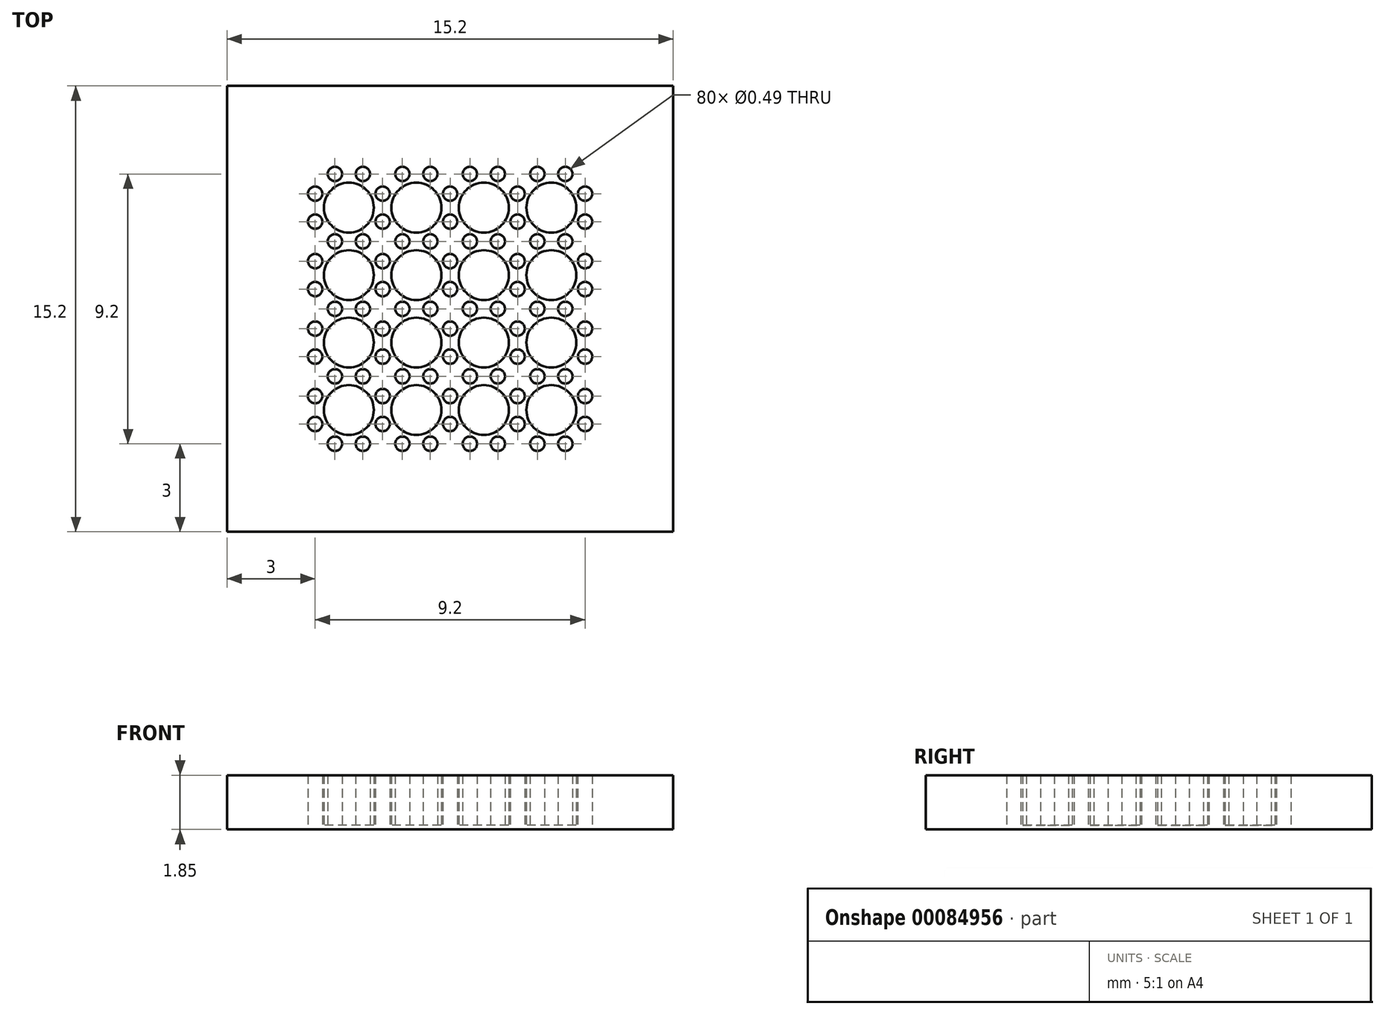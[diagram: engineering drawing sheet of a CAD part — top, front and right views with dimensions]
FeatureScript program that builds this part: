
annotation { "Feature Type Name" : "Feature", "Feature Type Description" : "" }
export const myFeature = defineFeature(function(context is Context, id is Id, definition is map)
    precondition{}
    {
        {
            var Q0;
            Q0=qCreatedBy(makeId("Top.planeOp"),FACE);
            var sketch = newSketch(context, id + "F0", { "sketchPlane" : qUnion([Q0])});
            skCircle(sketch, "E0", {"center": v(0, 0) * mm, "radius": 0.85 * mm});
            skPoint(sketch, "E1.0.midPoint", {"position": v(0, -1.15) * mm});
            skCircle(sketch, "E2", {"center": v(0.48, -1.15) * mm, "radius": 0.24 * mm});
            skCircle(sketch, "E3.1.0", {"center": v(1.15, -0.48) * mm, "radius": 0.24 * mm});
            skCircle(sketch, "E3.2.0", {"center": v(1.15, 0.48) * mm, "radius": 0.24 * mm});
            skCircle(sketch, "E3.3.0", {"center": v(0.48, 1.15) * mm, "radius": 0.24 * mm});
            skCircle(sketch, "E3.4.0", {"center": v(-0.48, 1.15) * mm, "radius": 0.24 * mm});
            skCircle(sketch, "E3.5.0", {"center": v(-1.15, 0.48) * mm, "radius": 0.24 * mm});
            skCircle(sketch, "E3.6.0", {"center": v(-1.15, -0.48) * mm, "radius": 0.24 * mm});
            skCircle(sketch, "E3.7.0", {"center": v(-0.48, -1.15) * mm, "radius": 0.24 * mm});
            skCircle(sketch, "E4.0.1.1", {"center": v(0, 2.3) * mm, "radius": 0.85 * mm});
            skCircle(sketch, "E4.0.1.2", {"center": v(-0.48, 3.45) * mm, "radius": 0.24 * mm});
            skCircle(sketch, "E4.0.1.3", {"center": v(-1.15, 1.82) * mm, "radius": 0.24 * mm});
            skCircle(sketch, "E4.0.1.4", {"center": v(-1.15, 2.78) * mm, "radius": 0.24 * mm});
            skCircle(sketch, "E4.0.1.5", {"center": v(1.15, 2.78) * mm, "radius": 0.24 * mm});
            skPoint(sketch, "E4.0.1.6", {"position": v(0, 1.15) * mm});
            skPoint(sketch, "E4.0.1.7", {"position": v(0, 2.3) * mm});
            skCircle(sketch, "E4.0.1.9", {"center": v(1.15, 1.82) * mm, "radius": 0.24 * mm});
            skCircle(sketch, "E4.0.1.10", {"center": v(0.48, 3.45) * mm, "radius": 0.24 * mm});
            skCircle(sketch, "E4.0.2.0", {"center": v(-0.48, 3.45) * mm, "radius": 0.24 * mm});
            skCircle(sketch, "E4.0.2.1", {"center": v(0, 4.6) * mm, "radius": 0.85 * mm});
            skCircle(sketch, "E4.0.2.2", {"center": v(-0.48, 5.75) * mm, "radius": 0.24 * mm});
            skCircle(sketch, "E4.0.2.3", {"center": v(-1.15, 4.12) * mm, "radius": 0.24 * mm});
            skCircle(sketch, "E4.0.2.4", {"center": v(-1.15, 5.08) * mm, "radius": 0.24 * mm});
            skCircle(sketch, "E4.0.2.5", {"center": v(1.15, 5.08) * mm, "radius": 0.24 * mm});
            skPoint(sketch, "E4.0.2.6", {"position": v(0, 3.45) * mm});
            skPoint(sketch, "E4.0.2.7", {"position": v(0, 4.6) * mm});
            skCircle(sketch, "E4.0.2.8", {"center": v(0.48, 3.45) * mm, "radius": 0.24 * mm});
            skCircle(sketch, "E4.0.2.9", {"center": v(1.15, 4.12) * mm, "radius": 0.24 * mm});
            skCircle(sketch, "E4.0.2.10", {"center": v(0.48, 5.75) * mm, "radius": 0.24 * mm});
            skCircle(sketch, "E4.0.3.0", {"center": v(-0.48, 5.75) * mm, "radius": 0.24 * mm});
            skCircle(sketch, "E4.0.3.1", {"center": v(0, 6.9) * mm, "radius": 0.85 * mm});
            skCircle(sketch, "E4.0.3.2", {"center": v(-0.48, 8.05) * mm, "radius": 0.24 * mm});
            skCircle(sketch, "E4.0.3.3", {"center": v(-1.15, 6.42) * mm, "radius": 0.24 * mm});
            skCircle(sketch, "E4.0.3.4", {"center": v(-1.15, 7.38) * mm, "radius": 0.24 * mm});
            skCircle(sketch, "E4.0.3.5", {"center": v(1.15, 7.38) * mm, "radius": 0.24 * mm});
            skPoint(sketch, "E4.0.3.6", {"position": v(0, 5.75) * mm});
            skPoint(sketch, "E4.0.3.7", {"position": v(0, 6.9) * mm});
            skCircle(sketch, "E4.0.3.8", {"center": v(0.48, 5.75) * mm, "radius": 0.24 * mm});
            skCircle(sketch, "E4.0.3.9", {"center": v(1.15, 6.42) * mm, "radius": 0.24 * mm});
            skCircle(sketch, "E4.0.3.10", {"center": v(0.48, 8.05) * mm, "radius": 0.24 * mm});
            skCircle(sketch, "E4.1.0.0", {"center": v(1.82, -1.15) * mm, "radius": 0.24 * mm});
            skCircle(sketch, "E4.1.0.1", {"center": v(2.3, 0) * mm, "radius": 0.85 * mm});
            skCircle(sketch, "E4.1.0.2", {"center": v(1.82, 1.15) * mm, "radius": 0.24 * mm});
            skCircle(sketch, "E4.1.0.5", {"center": v(3.45, 0.48) * mm, "radius": 0.24 * mm});
            skPoint(sketch, "E4.1.0.6", {"position": v(2.3, -1.15) * mm});
            skPoint(sketch, "E4.1.0.7", {"position": v(2.3, 0) * mm});
            skCircle(sketch, "E4.1.0.8", {"center": v(2.78, -1.15) * mm, "radius": 0.24 * mm});
            skCircle(sketch, "E4.1.0.9", {"center": v(3.45, -0.48) * mm, "radius": 0.24 * mm});
            skCircle(sketch, "E4.1.0.10", {"center": v(2.78, 1.15) * mm, "radius": 0.24 * mm});
            skCircle(sketch, "E4.1.1.0", {"center": v(1.82, 1.15) * mm, "radius": 0.24 * mm});
            skCircle(sketch, "E4.1.1.1", {"center": v(2.3, 2.3) * mm, "radius": 0.85 * mm});
            skCircle(sketch, "E4.1.1.2", {"center": v(1.82, 3.45) * mm, "radius": 0.24 * mm});
            skCircle(sketch, "E4.1.1.3", {"center": v(1.15, 1.82) * mm, "radius": 0.24 * mm});
            skCircle(sketch, "E4.1.1.4", {"center": v(1.15, 2.78) * mm, "radius": 0.24 * mm});
            skCircle(sketch, "E4.1.1.5", {"center": v(3.45, 2.78) * mm, "radius": 0.24 * mm});
            skPoint(sketch, "E4.1.1.6", {"position": v(2.3, 1.15) * mm});
            skPoint(sketch, "E4.1.1.7", {"position": v(2.3, 2.3) * mm});
            skCircle(sketch, "E4.1.1.8", {"center": v(2.78, 1.15) * mm, "radius": 0.24 * mm});
            skCircle(sketch, "E4.1.1.9", {"center": v(3.45, 1.82) * mm, "radius": 0.24 * mm});
            skCircle(sketch, "E4.1.1.10", {"center": v(2.78, 3.45) * mm, "radius": 0.24 * mm});
            skCircle(sketch, "E4.1.2.0", {"center": v(1.82, 3.45) * mm, "radius": 0.24 * mm});
            skCircle(sketch, "E4.1.2.1", {"center": v(2.3, 4.6) * mm, "radius": 0.85 * mm});
            skCircle(sketch, "E4.1.2.2", {"center": v(1.82, 5.75) * mm, "radius": 0.24 * mm});
            skCircle(sketch, "E4.1.2.3", {"center": v(1.15, 4.12) * mm, "radius": 0.24 * mm});
            skCircle(sketch, "E4.1.2.4", {"center": v(1.15, 5.08) * mm, "radius": 0.24 * mm});
            skCircle(sketch, "E4.1.2.5", {"center": v(3.45, 5.08) * mm, "radius": 0.24 * mm});
            skPoint(sketch, "E4.1.2.6", {"position": v(2.3, 3.45) * mm});
            skPoint(sketch, "E4.1.2.7", {"position": v(2.3, 4.6) * mm});
            skCircle(sketch, "E4.1.2.8", {"center": v(2.78, 3.45) * mm, "radius": 0.24 * mm});
            skCircle(sketch, "E4.1.2.9", {"center": v(3.45, 4.12) * mm, "radius": 0.24 * mm});
            skCircle(sketch, "E4.1.2.10", {"center": v(2.78, 5.75) * mm, "radius": 0.24 * mm});
            skCircle(sketch, "E4.1.3.0", {"center": v(1.82, 5.75) * mm, "radius": 0.24 * mm});
            skCircle(sketch, "E4.1.3.1", {"center": v(2.3, 6.9) * mm, "radius": 0.85 * mm});
            skCircle(sketch, "E4.1.3.2", {"center": v(1.82, 8.05) * mm, "radius": 0.24 * mm});
            skCircle(sketch, "E4.1.3.3", {"center": v(1.15, 6.42) * mm, "radius": 0.24 * mm});
            skCircle(sketch, "E4.1.3.4", {"center": v(1.15, 7.38) * mm, "radius": 0.24 * mm});
            skCircle(sketch, "E4.1.3.5", {"center": v(3.45, 7.38) * mm, "radius": 0.24 * mm});
            skPoint(sketch, "E4.1.3.6", {"position": v(2.3, 5.75) * mm});
            skPoint(sketch, "E4.1.3.7", {"position": v(2.3, 6.9) * mm});
            skCircle(sketch, "E4.1.3.8", {"center": v(2.78, 5.75) * mm, "radius": 0.24 * mm});
            skCircle(sketch, "E4.1.3.9", {"center": v(3.45, 6.42) * mm, "radius": 0.24 * mm});
            skCircle(sketch, "E4.1.3.10", {"center": v(2.78, 8.05) * mm, "radius": 0.24 * mm});
            skCircle(sketch, "E4.2.0.0", {"center": v(4.12, -1.15) * mm, "radius": 0.24 * mm});
            skCircle(sketch, "E4.2.0.1", {"center": v(4.6, 0) * mm, "radius": 0.85 * mm});
            skCircle(sketch, "E4.2.0.2", {"center": v(4.12, 1.15) * mm, "radius": 0.24 * mm});
            skCircle(sketch, "E4.2.0.3", {"center": v(3.45, -0.48) * mm, "radius": 0.24 * mm});
            skCircle(sketch, "E4.2.0.4", {"center": v(3.45, 0.48) * mm, "radius": 0.24 * mm});
            skCircle(sketch, "E4.2.0.5", {"center": v(5.75, 0.48) * mm, "radius": 0.24 * mm});
            skPoint(sketch, "E4.2.0.6", {"position": v(4.6, -1.15) * mm});
            skPoint(sketch, "E4.2.0.7", {"position": v(4.6, 0) * mm});
            skCircle(sketch, "E4.2.0.8", {"center": v(5.08, -1.15) * mm, "radius": 0.24 * mm});
            skCircle(sketch, "E4.2.0.9", {"center": v(5.75, -0.48) * mm, "radius": 0.24 * mm});
            skCircle(sketch, "E4.2.0.10", {"center": v(5.08, 1.15) * mm, "radius": 0.24 * mm});
            skCircle(sketch, "E4.2.1.0", {"center": v(4.12, 1.15) * mm, "radius": 0.24 * mm});
            skCircle(sketch, "E4.2.1.1", {"center": v(4.6, 2.3) * mm, "radius": 0.85 * mm});
            skCircle(sketch, "E4.2.1.2", {"center": v(4.12, 3.45) * mm, "radius": 0.24 * mm});
            skCircle(sketch, "E4.2.1.3", {"center": v(3.45, 1.82) * mm, "radius": 0.24 * mm});
            skCircle(sketch, "E4.2.1.4", {"center": v(3.45, 2.78) * mm, "radius": 0.24 * mm});
            skCircle(sketch, "E4.2.1.5", {"center": v(5.75, 2.78) * mm, "radius": 0.24 * mm});
            skPoint(sketch, "E4.2.1.6", {"position": v(4.6, 1.15) * mm});
            skPoint(sketch, "E4.2.1.7", {"position": v(4.6, 2.3) * mm});
            skCircle(sketch, "E4.2.1.8", {"center": v(5.08, 1.15) * mm, "radius": 0.24 * mm});
            skCircle(sketch, "E4.2.1.9", {"center": v(5.75, 1.82) * mm, "radius": 0.24 * mm});
            skCircle(sketch, "E4.2.1.10", {"center": v(5.08, 3.45) * mm, "radius": 0.24 * mm});
            skCircle(sketch, "E4.2.2.0", {"center": v(4.12, 3.45) * mm, "radius": 0.24 * mm});
            skCircle(sketch, "E4.2.2.1", {"center": v(4.6, 4.6) * mm, "radius": 0.85 * mm});
            skCircle(sketch, "E4.2.2.2", {"center": v(4.12, 5.75) * mm, "radius": 0.24 * mm});
            skCircle(sketch, "E4.2.2.3", {"center": v(3.45, 4.12) * mm, "radius": 0.24 * mm});
            skCircle(sketch, "E4.2.2.4", {"center": v(3.45, 5.08) * mm, "radius": 0.24 * mm});
            skCircle(sketch, "E4.2.2.5", {"center": v(5.75, 5.08) * mm, "radius": 0.24 * mm});
            skPoint(sketch, "E4.2.2.6", {"position": v(4.6, 3.45) * mm});
            skPoint(sketch, "E4.2.2.7", {"position": v(4.6, 4.6) * mm});
            skCircle(sketch, "E4.2.2.8", {"center": v(5.08, 3.45) * mm, "radius": 0.24 * mm});
            skCircle(sketch, "E4.2.2.9", {"center": v(5.75, 4.12) * mm, "radius": 0.24 * mm});
            skCircle(sketch, "E4.2.2.10", {"center": v(5.08, 5.75) * mm, "radius": 0.24 * mm});
            skCircle(sketch, "E4.2.3.0", {"center": v(4.12, 5.75) * mm, "radius": 0.24 * mm});
            skCircle(sketch, "E4.2.3.1", {"center": v(4.6, 6.9) * mm, "radius": 0.85 * mm});
            skCircle(sketch, "E4.2.3.2", {"center": v(4.12, 8.05) * mm, "radius": 0.24 * mm});
            skCircle(sketch, "E4.2.3.3", {"center": v(3.45, 6.42) * mm, "radius": 0.24 * mm});
            skCircle(sketch, "E4.2.3.4", {"center": v(3.45, 7.38) * mm, "radius": 0.24 * mm});
            skCircle(sketch, "E4.2.3.5", {"center": v(5.75, 7.38) * mm, "radius": 0.24 * mm});
            skPoint(sketch, "E4.2.3.6", {"position": v(4.6, 5.75) * mm});
            skPoint(sketch, "E4.2.3.7", {"position": v(4.6, 6.9) * mm});
            skCircle(sketch, "E4.2.3.8", {"center": v(5.08, 5.75) * mm, "radius": 0.24 * mm});
            skCircle(sketch, "E4.2.3.9", {"center": v(5.75, 6.42) * mm, "radius": 0.24 * mm});
            skCircle(sketch, "E4.2.3.10", {"center": v(5.08, 8.05) * mm, "radius": 0.24 * mm});
            skCircle(sketch, "E4.3.0.0", {"center": v(6.42, -1.15) * mm, "radius": 0.24 * mm});
            skCircle(sketch, "E4.3.0.1", {"center": v(6.9, 0) * mm, "radius": 0.85 * mm});
            skCircle(sketch, "E4.3.0.2", {"center": v(6.42, 1.15) * mm, "radius": 0.24 * mm});
            skCircle(sketch, "E4.3.0.3", {"center": v(5.75, -0.48) * mm, "radius": 0.24 * mm});
            skCircle(sketch, "E4.3.0.4", {"center": v(5.75, 0.48) * mm, "radius": 0.24 * mm});
            skCircle(sketch, "E4.3.0.5", {"center": v(8.05, 0.48) * mm, "radius": 0.24 * mm});
            skPoint(sketch, "E4.3.0.6", {"position": v(6.9, -1.15) * mm});
            skPoint(sketch, "E4.3.0.7", {"position": v(6.9, 0) * mm});
            skCircle(sketch, "E4.3.0.8", {"center": v(7.38, -1.15) * mm, "radius": 0.24 * mm});
            skCircle(sketch, "E4.3.0.9", {"center": v(8.05, -0.48) * mm, "radius": 0.24 * mm});
            skCircle(sketch, "E4.3.0.10", {"center": v(7.38, 1.15) * mm, "radius": 0.24 * mm});
            skCircle(sketch, "E4.3.1.0", {"center": v(6.42, 1.15) * mm, "radius": 0.24 * mm});
            skCircle(sketch, "E4.3.1.1", {"center": v(6.9, 2.3) * mm, "radius": 0.85 * mm});
            skCircle(sketch, "E4.3.1.2", {"center": v(6.42, 3.45) * mm, "radius": 0.24 * mm});
            skCircle(sketch, "E4.3.1.3", {"center": v(5.75, 1.82) * mm, "radius": 0.24 * mm});
            skCircle(sketch, "E4.3.1.4", {"center": v(5.75, 2.78) * mm, "radius": 0.24 * mm});
            skCircle(sketch, "E4.3.1.5", {"center": v(8.05, 2.78) * mm, "radius": 0.24 * mm});
            skPoint(sketch, "E4.3.1.6", {"position": v(6.9, 1.15) * mm});
            skPoint(sketch, "E4.3.1.7", {"position": v(6.9, 2.3) * mm});
            skCircle(sketch, "E4.3.1.8", {"center": v(7.38, 1.15) * mm, "radius": 0.24 * mm});
            skCircle(sketch, "E4.3.1.9", {"center": v(8.05, 1.82) * mm, "radius": 0.24 * mm});
            skCircle(sketch, "E4.3.1.10", {"center": v(7.38, 3.45) * mm, "radius": 0.24 * mm});
            skCircle(sketch, "E4.3.2.0", {"center": v(6.42, 3.45) * mm, "radius": 0.24 * mm});
            skCircle(sketch, "E4.3.2.1", {"center": v(6.9, 4.6) * mm, "radius": 0.85 * mm});
            skCircle(sketch, "E4.3.2.2", {"center": v(6.42, 5.75) * mm, "radius": 0.24 * mm});
            skCircle(sketch, "E4.3.2.3", {"center": v(5.75, 4.12) * mm, "radius": 0.24 * mm});
            skCircle(sketch, "E4.3.2.4", {"center": v(5.75, 5.08) * mm, "radius": 0.24 * mm});
            skCircle(sketch, "E4.3.2.5", {"center": v(8.05, 5.08) * mm, "radius": 0.24 * mm});
            skPoint(sketch, "E4.3.2.6", {"position": v(6.9, 3.45) * mm});
            skPoint(sketch, "E4.3.2.7", {"position": v(6.9, 4.6) * mm});
            skCircle(sketch, "E4.3.2.8", {"center": v(7.38, 3.45) * mm, "radius": 0.24 * mm});
            skCircle(sketch, "E4.3.2.9", {"center": v(8.05, 4.12) * mm, "radius": 0.24 * mm});
            skCircle(sketch, "E4.3.2.10", {"center": v(7.38, 5.75) * mm, "radius": 0.24 * mm});
            skCircle(sketch, "E4.3.3.0", {"center": v(6.42, 5.75) * mm, "radius": 0.24 * mm});
            skCircle(sketch, "E4.3.3.1", {"center": v(6.9, 6.9) * mm, "radius": 0.85 * mm});
            skCircle(sketch, "E4.3.3.2", {"center": v(6.42, 8.05) * mm, "radius": 0.24 * mm});
            skCircle(sketch, "E4.3.3.3", {"center": v(5.75, 6.42) * mm, "radius": 0.24 * mm});
            skCircle(sketch, "E4.3.3.4", {"center": v(5.75, 7.38) * mm, "radius": 0.24 * mm});
            skCircle(sketch, "E4.3.3.5", {"center": v(8.05, 7.38) * mm, "radius": 0.24 * mm});
            skPoint(sketch, "E4.3.3.6", {"position": v(6.9, 5.75) * mm});
            skPoint(sketch, "E4.3.3.7", {"position": v(6.9, 6.9) * mm});
            skCircle(sketch, "E4.3.3.8", {"center": v(7.38, 5.75) * mm, "radius": 0.24 * mm});
            skCircle(sketch, "E4.3.3.9", {"center": v(8.05, 6.42) * mm, "radius": 0.24 * mm});
            skCircle(sketch, "E4.3.3.10", {"center": v(7.38, 8.05) * mm, "radius": 0.24 * mm});
            skLineSegment(sketch, "E4.direction1", {"start": v(-0.48, -1.15) * mm, "end": v(1.82, -1.15) * mm, "construction": true});
            skLineSegment(sketch, "E4.direction2", {"start": v(-0.48, -1.15) * mm, "end": v(-0.48, 1.15) * mm, "construction": true});
            skLineSegment(sketch, "E5.bottom", {"start": v(-4.15, -4.15) * mm, "end": v(11.05, -4.15) * mm});
            skLineSegment(sketch, "E5.top", {"start": v(-4.15, 11.05) * mm, "end": v(11.05, 11.05) * mm});
            skLineSegment(sketch, "E5.left", {"start": v(-4.15, -4.15) * mm, "end": v(-4.15, 11.05) * mm});
            skLineSegment(sketch, "E5.right", {"start": v(11.05, -4.15) * mm, "end": v(11.05, 11.05) * mm});
            skSolve(sketch);
        }
        {
            var Q0;
            Q0 = qSketchRegion(id + "F0", true);
            extrude(context, id + "F1", {"entities" : qUnion([Q0]), "depth" : 1.85 * mm});
        }
        {
            var Q0;
            Q0=makeQuery(id+"F1.opExtrude","CAP_FACE",FACE,{"disambiguationData":[OSD([sQuery(id+"F0.wireOp",EDGE,"E0"),sQuery(id+"F0.wireOp",EDGE,"E2"),sQuery(id+"F0.wireOp",EDGE,"E3.5.0"),sQuery(id+"F0.wireOp",EDGE,"E3.6.0"),sQuery(id+"F0.wireOp",EDGE,"E3.7.0"),sQuery(id+"F0.wireOp",EDGE,"E3.4.0"),sQuery(id+"F0.wireOp",EDGE,"E4.0.1.1"),sQuery(id+"F0.wireOp",EDGE,"E4.0.1.3"),sQuery(id+"F0.wireOp",EDGE,"E4.0.1.4"),sQuery(id+"F0.wireOp",EDGE,"E3.3.0"),sQuery(id+"F0.wireOp",EDGE,"E4.0.2.0"),sQuery(id+"F0.wireOp",EDGE,"E4.0.2.1"),sQuery(id+"F0.wireOp",EDGE,"E4.0.2.3"),sQuery(id+"F0.wireOp",EDGE,"E4.0.2.4"),sQuery(id+"F0.wireOp",EDGE,"E4.0.2.8"),sQuery(id+"F0.wireOp",EDGE,"E4.0.3.0"),sQuery(id+"F0.wireOp",EDGE,"E4.0.3.1"),sQuery(id+"F0.wireOp",EDGE,"E4.0.3.2"),sQuery(id+"F0.wireOp",EDGE,"E4.0.3.3"),sQuery(id+"F0.wireOp",EDGE,"E4.0.3.4"),sQuery(id+"F0.wireOp",EDGE,"E4.0.3.8"),sQuery(id+"F0.wireOp",EDGE,"E4.0.3.10"),sQuery(id+"F0.wireOp",EDGE,"E4.1.0.0"),sQuery(id+"F0.wireOp",EDGE,"E4.1.0.1"),sQuery(id+"F0.wireOp",EDGE,"E3.1.0"),sQuery(id+"F0.wireOp",EDGE,"E3.2.0"),sQuery(id+"F0.wireOp",EDGE,"E4.1.0.8"),sQuery(id+"F0.wireOp",EDGE,"E4.1.1.0"),sQuery(id+"F0.wireOp",EDGE,"E4.1.1.1"),sQuery(id+"F0.wireOp",EDGE,"E4.1.1.3"),sQuery(id+"F0.wireOp",EDGE,"E4.1.1.4"),sQuery(id+"F0.wireOp",EDGE,"E4.1.1.8"),sQuery(id+"F0.wireOp",EDGE,"E4.1.2.0"),sQuery(id+"F0.wireOp",EDGE,"E4.1.2.1"),sQuery(id+"F0.wireOp",EDGE,"E4.1.2.3"),sQuery(id+"F0.wireOp",EDGE,"E4.1.2.4"),sQuery(id+"F0.wireOp",EDGE,"E4.1.2.8"),sQuery(id+"F0.wireOp",EDGE,"E4.1.3.0"),sQuery(id+"F0.wireOp",EDGE,"E4.1.3.1"),sQuery(id+"F0.wireOp",EDGE,"E4.1.3.2"),sQuery(id+"F0.wireOp",EDGE,"E4.1.3.3"),sQuery(id+"F0.wireOp",EDGE,"E4.1.3.4"),sQuery(id+"F0.wireOp",EDGE,"E4.1.3.8"),sQuery(id+"F0.wireOp",EDGE,"E4.1.3.10"),sQuery(id+"F0.wireOp",EDGE,"E4.2.0.0"),sQuery(id+"F0.wireOp",EDGE,"E4.2.0.1"),sQuery(id+"F0.wireOp",EDGE,"E4.2.0.3"),sQuery(id+"F0.wireOp",EDGE,"E4.2.0.4"),sQuery(id+"F0.wireOp",EDGE,"E4.2.0.8"),sQuery(id+"F0.wireOp",EDGE,"E4.2.1.0"),sQuery(id+"F0.wireOp",EDGE,"E4.2.1.1"),sQuery(id+"F0.wireOp",EDGE,"E4.2.1.3"),sQuery(id+"F0.wireOp",EDGE,"E4.2.1.4"),sQuery(id+"F0.wireOp",EDGE,"E4.2.1.8"),sQuery(id+"F0.wireOp",EDGE,"E4.2.2.0"),sQuery(id+"F0.wireOp",EDGE,"E4.2.2.1"),sQuery(id+"F0.wireOp",EDGE,"E4.2.2.3"),sQuery(id+"F0.wireOp",EDGE,"E4.2.2.4"),sQuery(id+"F0.wireOp",EDGE,"E4.2.2.8"),sQuery(id+"F0.wireOp",EDGE,"E4.2.3.0"),sQuery(id+"F0.wireOp",EDGE,"E4.2.3.1"),sQuery(id+"F0.wireOp",EDGE,"E4.2.3.2"),sQuery(id+"F0.wireOp",EDGE,"E4.2.3.3"),sQuery(id+"F0.wireOp",EDGE,"E4.2.3.4"),sQuery(id+"F0.wireOp",EDGE,"E4.2.3.8"),sQuery(id+"F0.wireOp",EDGE,"E4.2.3.10"),sQuery(id+"F0.wireOp",EDGE,"E4.3.0.0"),sQuery(id+"F0.wireOp",EDGE,"E4.3.0.1"),sQuery(id+"F0.wireOp",EDGE,"E4.3.0.3"),sQuery(id+"F0.wireOp",EDGE,"E4.3.0.4"),sQuery(id+"F0.wireOp",EDGE,"E4.3.0.5"),sQuery(id+"F0.wireOp",EDGE,"E4.3.0.8"),sQuery(id+"F0.wireOp",EDGE,"E4.3.0.9"),sQuery(id+"F0.wireOp",EDGE,"E4.3.1.0"),sQuery(id+"F0.wireOp",EDGE,"E4.3.1.1"),sQuery(id+"F0.wireOp",EDGE,"E4.3.1.3"),sQuery(id+"F0.wireOp",EDGE,"E4.3.1.4"),sQuery(id+"F0.wireOp",EDGE,"E4.3.1.5"),sQuery(id+"F0.wireOp",EDGE,"E4.3.1.8"),sQuery(id+"F0.wireOp",EDGE,"E4.3.1.9"),sQuery(id+"F0.wireOp",EDGE,"E4.3.2.0"),sQuery(id+"F0.wireOp",EDGE,"E4.3.2.1"),sQuery(id+"F0.wireOp",EDGE,"E4.3.2.3"),sQuery(id+"F0.wireOp",EDGE,"E4.3.2.4"),sQuery(id+"F0.wireOp",EDGE,"E4.3.2.5"),sQuery(id+"F0.wireOp",EDGE,"E4.3.2.8"),sQuery(id+"F0.wireOp",EDGE,"E4.3.2.9"),sQuery(id+"F0.wireOp",EDGE,"E4.3.3.0"),sQuery(id+"F0.wireOp",EDGE,"E4.3.3.1"),sQuery(id+"F0.wireOp",EDGE,"E4.3.3.2"),sQuery(id+"F0.wireOp",EDGE,"E4.3.3.3"),sQuery(id+"F0.wireOp",EDGE,"E4.3.3.4"),sQuery(id+"F0.wireOp",EDGE,"E4.3.3.5"),sQuery(id+"F0.wireOp",EDGE,"E4.3.3.8"),sQuery(id+"F0.wireOp",EDGE,"E4.3.3.9"),sQuery(id+"F0.wireOp",EDGE,"E4.3.3.10"),sQuery(id+"F0.wireOp",EDGE,"E5.bottom"),sQuery(id+"F0.wireOp",EDGE,"E5.top"),sQuery(id+"F0.wireOp",EDGE,"E5.left"),sQuery(id+"F0.wireOp",EDGE,"E5.right")])],"isStart":true});
            var sketch = newSketch(context, id + "F2", { "sketchPlane" : qUnion([Q0])});
            skCircle(sketch, "E6.0", {"center": v(0, 0) * mm, "radius": 0.85 * mm});
            skCircle(sketch, "E6.1", {"center": v(2.3, 0) * mm, "radius": 0.85 * mm});
            skCircle(sketch, "E6.2", {"center": v(4.6, 0) * mm, "radius": 0.85 * mm});
            skCircle(sketch, "E6.3", {"center": v(6.9, 0) * mm, "radius": 0.85 * mm});
            skCircle(sketch, "E7.0", {"center": v(0, -2.3) * mm, "radius": 0.85 * mm});
            skCircle(sketch, "E7.1", {"center": v(2.3, -2.3) * mm, "radius": 0.85 * mm});
            skCircle(sketch, "E7.2", {"center": v(4.6, -2.3) * mm, "radius": 0.85 * mm});
            skCircle(sketch, "E7.3", {"center": v(6.9, -2.3) * mm, "radius": 0.85 * mm});
            skCircle(sketch, "E7.4", {"center": v(6.9, -4.6) * mm, "radius": 0.85 * mm});
            skCircle(sketch, "E7.5", {"center": v(4.6, -4.6) * mm, "radius": 0.85 * mm});
            skCircle(sketch, "E7.6", {"center": v(2.3, -4.6) * mm, "radius": 0.85 * mm});
            skCircle(sketch, "E7.7", {"center": v(0, -4.6) * mm, "radius": 0.85 * mm});
            skCircle(sketch, "E7.8", {"center": v(0, -6.9) * mm, "radius": 0.85 * mm});
            skCircle(sketch, "E7.9", {"center": v(2.3, -6.9) * mm, "radius": 0.85 * mm});
            skCircle(sketch, "E7.10", {"center": v(4.6, -6.9) * mm, "radius": 0.85 * mm});
            skCircle(sketch, "E7.11", {"center": v(6.9, -6.9) * mm, "radius": 0.85 * mm});
            skSolve(sketch);
        }
        {
            var Q0;
            Q0 = qSketchRegion(id + "F2", true);
            extrude(context, id + "F3", {"entities" : qUnion([Q0]), "operationType" : NewBodyOperationType.ADD, "oppositeDirection" : true, "depth" : 0.15 * mm});
        }
    });
